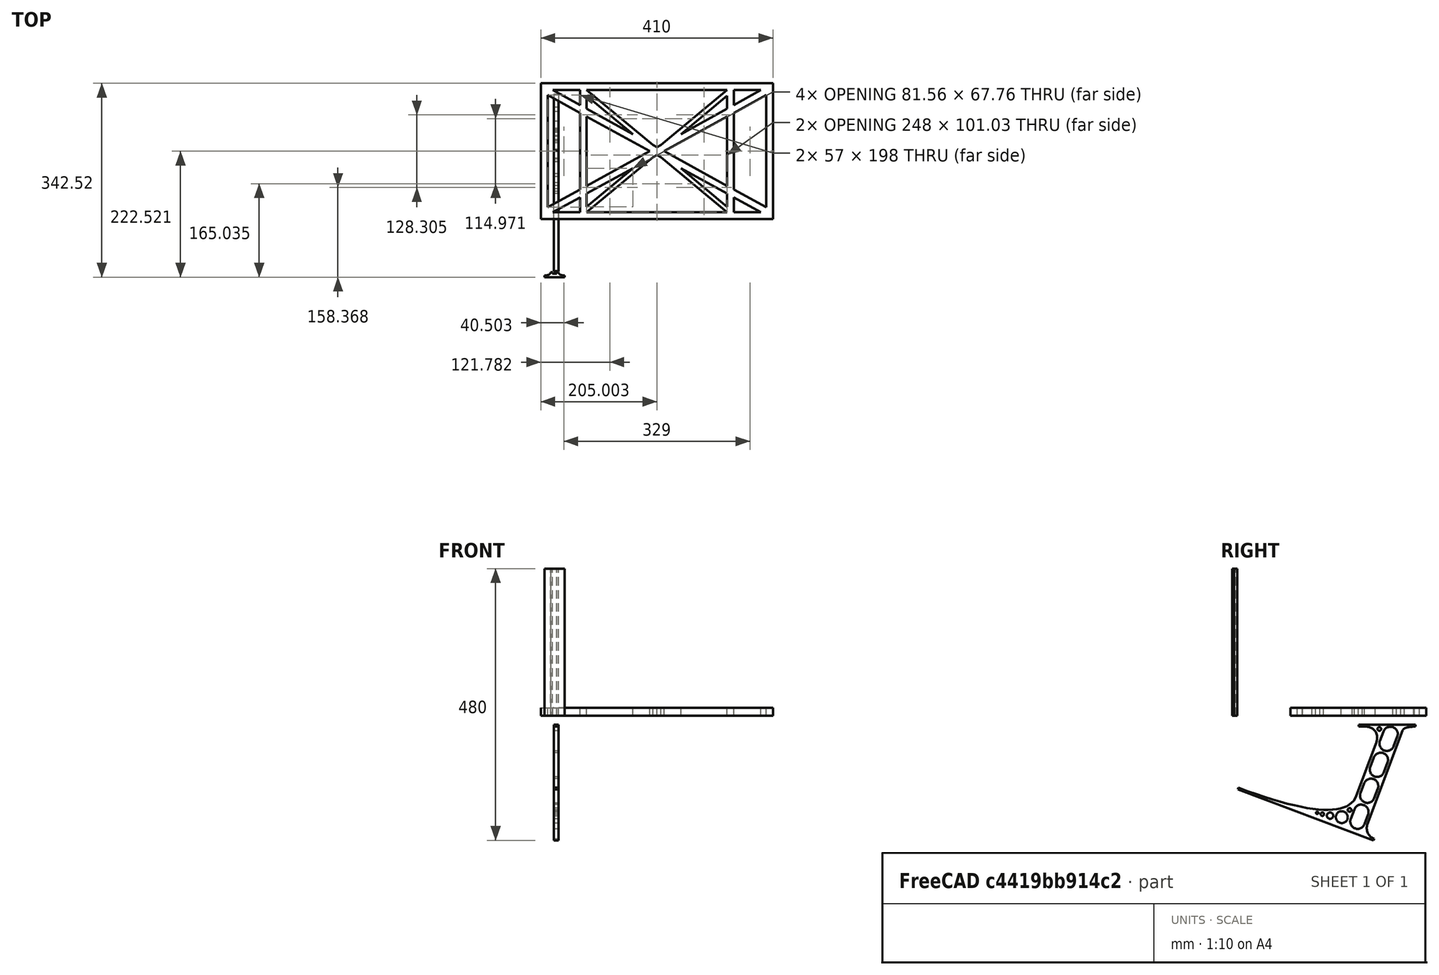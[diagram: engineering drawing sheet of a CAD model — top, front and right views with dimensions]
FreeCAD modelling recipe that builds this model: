
FCSTD DOCUMENT  (FreeCAD 0.19R0.19.2)
Label: laptopStand054
License: All rights reserved
LicenseURL: http://en.wikipedia.org/wiki/All_rights_reserved
objects: Sketcher::SketchObject×3, Part::Extrusion×3
note: 6 computed .brp shape members not serialized (recipe doc carries the construction recipe); baked Part::Feature solids carry a one-line shape summary decoded from their .brp

FEATURE [Sketcher::SketchObject] Sketch
  FullyConstrained = false
  sketch-geometry (92):
    g0: LineSegment StartX=-22.9272 StartY=136.221 StartZ=0 EndX=387.073 EndY=136.221 EndZ=0
    g1: LineSegment StartX=-22.9272 StartY=-103.779 StartZ=0 EndX=387.073 EndY=-103.779 EndZ=0
    g2: LineSegment StartX=375.073 StartY=115.221 StartZ=0 EndX=318.073 EndY=83.9235 EndZ=0
    g3: LineSegment StartX=-10.9272 StartY=-82.7794 StartZ=0 EndX=46.0728 EndY=-51.4823 EndZ=0
    g4: LineSegment StartX=-1.92719 StartY=124.221 StartZ=0 EndX=46.0728 EndY=97.8651 EndZ=0
    g5: LineSegment StartX=366.073 StartY=-91.7794 StartZ=0 EndX=318.073 EndY=-65.424 EndZ=0
    g6: LineSegment StartX=-10.9272 StartY=115.221 StartZ=0 EndX=-10.9272 EndY=-82.7794 EndZ=0
    g7: LineSegment StartX=375.073 StartY=-82.7794 StartZ=0 EndX=375.073 EndY=115.221 EndZ=0
    g8: LineSegment StartX=-1.92719 StartY=-91.7794 StartZ=0 EndX=46.0728 EndY=-91.7794 EndZ=0
    g9: LineSegment StartX=318.073 StartY=124.221 StartZ=0 EndX=366.073 EndY=124.221 EndZ=0
    g10: LineSegment StartX=306.073 StartY=-81.8102 StartZ=0 EndX=224.513 EndY=-14.0532 EndZ=0
    g11: LineSegment StartX=58.0728 StartY=114.251 StartZ=0 EndX=139.632 EndY=46.4944 EndZ=0
    g12: LineSegment StartX=306.073 StartY=124.221 StartZ=0 EndX=189.124 EndY=27.0628 EndZ=0
    g13: LineSegment StartX=58.0728 StartY=-91.7794 StartZ=0 EndX=175.022 EndY=5.37834 EndZ=0
    g14: LineSegment StartX=46.0728 StartY=124.221 StartZ=0 EndX=46.0728 EndY=97.8651 EndZ=0
    g15: LineSegment StartX=58.0728 StartY=-81.8102 StartZ=0 EndX=58.0728 EndY=-58.8351 EndZ=0
    g16: LineSegment StartX=318.073 StartY=124.221 StartZ=0 EndX=318.073 EndY=97.8651 EndZ=0
    g17: LineSegment StartX=306.073 StartY=114.251 StartZ=0 EndX=306.073 EndY=91.2763 EndZ=0
    g18: LineSegment StartX=224.513 StartY=46.4944 StartZ=0 EndX=306.073 EndY=114.251 EndZ=0
    g19: LineSegment StartX=175.022 StartY=27.0628 StartZ=0 EndX=58.0728 EndY=124.221 EndZ=0
    g20: LineSegment StartX=169.377 StartY=16.2206 StartZ=0 EndX=58.0728 EndY=77.3346 EndZ=0
    g21: LineSegment StartX=139.632 StartY=-14.0532 StartZ=0 EndX=58.0728 EndY=-81.8102 EndZ=0
    g22: LineSegment StartX=194.768 StartY=16.2206 StartZ=0 EndX=306.073 EndY=-44.8935 EndZ=0
    g23: LineSegment StartX=224.513 StartY=46.4944 StartZ=0 EndX=306.073 EndY=91.2763 EndZ=0
    g24: LineSegment StartX=139.632 StartY=-14.0532 StartZ=0 EndX=58.0728 EndY=-58.8351 EndZ=0
    g25: LineSegment StartX=189.124 StartY=5.37834 StartZ=0 EndX=306.073 EndY=-91.7794 EndZ=0
    g26: LineSegment StartX=306.073 StartY=77.3346 StartZ=0 EndX=306.073 EndY=-44.8935 EndZ=0
    g27: LineSegment StartX=318.073 StartY=83.9235 StartZ=0 EndX=318.073 EndY=-51.4823 EndZ=0
    g28: LineSegment StartX=318.073 StartY=97.8651 StartZ=0 EndX=366.073 EndY=124.221 EndZ=0
    g29: LineSegment StartX=306.073 StartY=77.3346 StartZ=0 EndX=194.768 EndY=16.2206 EndZ=0
    g30: LineSegment StartX=306.073 StartY=-58.8351 StartZ=0 EndX=224.513 EndY=-14.0532 EndZ=0
    g31: LineSegment StartX=306.073 StartY=-58.8351 StartZ=0 EndX=306.073 EndY=-81.8102 EndZ=0
    g32: LineSegment StartX=318.073 StartY=-51.4823 StartZ=0 EndX=375.073 EndY=-82.7794 EndZ=0
    g33: LineSegment StartX=318.073 StartY=-65.424 StartZ=0 EndX=318.073 EndY=-91.7794 EndZ=0
    g34: LineSegment StartX=318.073 StartY=-91.7794 StartZ=0 EndX=366.073 EndY=-91.7794 EndZ=0
    g35: LineSegment StartX=58.0728 StartY=-44.8935 StartZ=0 EndX=58.0728 EndY=77.3346 EndZ=0
    g36: LineSegment StartX=46.0728 StartY=-65.424 StartZ=0 EndX=-1.92719 EndY=-91.7794 EndZ=0
    g37: LineSegment StartX=46.0728 StartY=-65.424 StartZ=0 EndX=46.0728 EndY=-91.7794 EndZ=0
    g38: LineSegment StartX=58.0728 StartY=-44.8935 StartZ=0 EndX=169.377 EndY=16.2206 EndZ=0
    g39: LineSegment StartX=58.0728 StartY=91.2763 StartZ=0 EndX=58.0728 EndY=114.251 EndZ=0
    g40: LineSegment StartX=46.0728 StartY=83.9235 StartZ=0 EndX=46.0728 EndY=-51.4823 EndZ=0
    g41: LineSegment StartX=46.0728 StartY=124.221 StartZ=0 EndX=-1.92719 EndY=124.221 EndZ=0
    g42: LineSegment StartX=58.0728 StartY=91.2763 StartZ=0 EndX=139.632 EndY=46.4944 EndZ=0
    g43: LineSegment StartX=46.0728 StartY=83.9235 StartZ=0 EndX=-10.9272 EndY=115.221 EndZ=0
    g44: LineSegment StartX=-22.9272 StartY=136.221 StartZ=0 EndX=-42.9272 EndY=136.221 EndZ=0
    g45: LineSegment StartX=387.073 StartY=136.221 StartZ=0 EndX=407.073 EndY=136.221 EndZ=0
    g46: LineSegment StartX=-42.9272 StartY=136.221 StartZ=0 EndX=-42.9272 EndY=-103.779 EndZ=0
    g47: LineSegment StartX=-22.9272 StartY=-103.779 StartZ=0 EndX=-42.9272 EndY=-103.779 EndZ=0
    g48: LineSegment StartX=407.073 StartY=136.221 StartZ=0 EndX=407.073 EndY=-103.779 EndZ=0
    g49: LineSegment StartX=387.073 StartY=-103.779 StartZ=0 EndX=407.073 EndY=-103.779 EndZ=0
    g50: LineSegment StartX=179.022 StartY=27.0628 StartZ=0 EndX=179.022 EndY=124.221 EndZ=0
    g51: LineSegment StartX=185.124 StartY=27.0628 StartZ=0 EndX=185.124 EndY=124.221 EndZ=0
    g52: ArcOfCircle CenterX=-26.9272 CenterY=22.1087 CenterZ=0 NormalX=0 NormalY=0 NormalZ=1 AngleXU=0 Radius=8 StartAngle=1e-16 EndAngle=3.14159
    g53: ArcOfCircle CenterX=-26.9272 CenterY=-83.7794 CenterZ=0 NormalX=0 NormalY=0 NormalZ=1 AngleXU=0 Radius=8 StartAngle=3.14159 EndAngle=6.28319
    g54: LineSegment StartX=-34.9272 StartY=22.1087 StartZ=0 EndX=-34.9272 EndY=-83.7794 EndZ=0
    g55: LineSegment StartX=-18.9272 StartY=22.1087 StartZ=0 EndX=-18.9272 EndY=-83.7794 EndZ=0
    g56: LineSegment StartX=185.124 StartY=-91.7794 StartZ=0 EndX=306.073 EndY=-91.7794 EndZ=0
    g57: LineSegment StartX=179.022 StartY=-91.7794 StartZ=0 EndX=58.0728 EndY=-91.7794 EndZ=0
    g58: LineSegment StartX=306.073 StartY=124.221 StartZ=0 EndX=185.124 EndY=124.221 EndZ=0
    g59: LineSegment StartX=179.022 StartY=124.221 StartZ=0 EndX=58.0728 EndY=124.221 EndZ=0
    g60: ArcOfCircle CenterX=391.073 CenterY=22.1087 CenterZ=0 NormalX=0 NormalY=0 NormalZ=1 AngleXU=0 Radius=8 StartAngle=-4.4e-15 EndAngle=3.14159
    g61: LineSegment StartX=399.073 StartY=22.1087 StartZ=0 EndX=399.073 EndY=-83.7794 EndZ=0
    g62: LineSegment StartX=383.073 StartY=22.1087 StartZ=0 EndX=383.073 EndY=-83.7794 EndZ=0
    g63: ArcOfCircle CenterX=391.073 CenterY=-83.7794 CenterZ=0 NormalX=0 NormalY=0 NormalZ=1 AngleXU=0 Radius=8 StartAngle=3.14159 EndAngle=6.28319
    g64: Circle CenterX=175.022 CenterY=27.0628 CenterZ=0 NormalX=0 NormalY=0 NormalZ=1 AngleXU=0 Radius=1
    g65: Circle CenterX=179.022 CenterY=24.8665 CenterZ=0 NormalX=0 NormalY=0 NormalZ=1 AngleXU=0 Radius=1
    g66: Circle CenterX=179.022 CenterY=27.0628 CenterZ=0 NormalX=0 NormalY=0 NormalZ=1 AngleXU=0 Radius=1
    g67: BSplineCurve PolesCount=3 KnotsCount=2 Degree=2 IsPeriodic=0
    g68: GeomPoint X=175.022 Y=27.0628 Z=0
    g69: GeomPoint X=179.022 Y=27.0628 Z=0
    g70: Circle CenterX=189.124 CenterY=27.0628 CenterZ=0 NormalX=0 NormalY=0 NormalZ=1 AngleXU=0 Radius=1
    g71: Circle CenterX=185.124 CenterY=24.8665 CenterZ=0 NormalX=0 NormalY=0 NormalZ=1 AngleXU=0 Radius=1
    g72: Circle CenterX=185.124 CenterY=27.0628 CenterZ=0 NormalX=0 NormalY=0 NormalZ=1 AngleXU=0 Radius=1
    g73: BSplineCurve PolesCount=3 KnotsCount=2 Degree=2 IsPeriodic=0
    g74: GeomPoint X=189.124 Y=27.0628 Z=0
    g75: GeomPoint X=185.124 Y=27.0628 Z=0
    g76: Circle CenterX=175.022 CenterY=5.37834 CenterZ=0 NormalX=0 NormalY=0 NormalZ=1 AngleXU=0 Radius=1
    g77: Circle CenterX=179.022 CenterY=7.57463 CenterZ=0 NormalX=0 NormalY=0 NormalZ=1 AngleXU=0 Radius=1
    g78: Circle CenterX=179.022 CenterY=5.34704 CenterZ=0 NormalX=0 NormalY=0 NormalZ=1 AngleXU=0 Radius=1
    g79: BSplineCurve PolesCount=3 KnotsCount=2 Degree=2 IsPeriodic=0
    g80: GeomPoint X=175.022 Y=5.37834 Z=0
    g81: GeomPoint X=179.022 Y=5.34704 Z=0
    g82: Circle CenterX=189.124 CenterY=5.37834 CenterZ=0 NormalX=0 NormalY=0 NormalZ=1 AngleXU=0 Radius=1
    g83: Circle CenterX=185.124 CenterY=7.57463 CenterZ=0 NormalX=0 NormalY=0 NormalZ=1 AngleXU=0 Radius=1
    g84: Circle CenterX=185.124 CenterY=5.34704 CenterZ=0 NormalX=0 NormalY=0 NormalZ=1 AngleXU=0 Radius=1
    g85: BSplineCurve PolesCount=3 KnotsCount=2 Degree=2 IsPeriodic=0
    g86: GeomPoint X=189.124 Y=5.37834 Z=0
    g87: GeomPoint X=185.124 Y=5.34704 Z=0
    g88: LineSegment StartX=179.022 StartY=5.34704 StartZ=0 EndX=179.022 EndY=-91.7794 EndZ=0
    g89: LineSegment StartX=185.124 StartY=-91.7794 StartZ=0 EndX=185.124 EndY=5.34704 EndZ=0
    g90: LineSegment StartX=165.377 StartY=16.2206 StartZ=0 EndX=169.377 EndY=16.2206 EndZ=0
    g91: LineSegment StartX=194.768 StartY=16.2206 StartZ=0 EndX=198.768 EndY=16.2206 EndZ=0
  constraints (182):
    c: Horizontal(g0)
    c: Distance(g0) = 410
    c: Horizontal(g1)
    c: Block(g0)
    c: Horizontal(g8)
    c: Horizontal(g9)
    c: Tangent(g5,g20)
    c: PointOnObject(g20,g3)
    c: PointOnObject(g22,g2)
    c: Coincident(g42,g11)
    c: Coincident(g18,g23)
    c: Coincident(g24,g21)
    c: Coincident(g30,g10)
    c: Coincident(g18,g17)
    c: Tangent(g17,g26)
    c: Tangent(g16,g27)
    c: Coincident(g23,g17)
    c: Tangent(g23,g28)
    c: Coincident(g2,g27)
    c: Coincident(g29,g26)
    c: Tangent(g2,g29)
    c: Coincident(g31,g10)
    c: Tangent(g5,g30)
    c: Tangent(g26,g31)
    c: Coincident(g22,g26)
    c: Tangent(g22,g32)
    c: Coincident(g27,g32)
    c: Coincident(g33,g5)
    c: Tangent(g27,g33)
    c: Coincident(g21,g15)
    c: Tangent(g15,g35)
    c: Coincident(g24,g15)
    c: Tangent(g24,g36)
    c: Coincident(g37,g36)
    c: Tangent(g14,g37)
    c: Coincident(g3,g40)
    c: Coincident(g38,g35)
    c: Tangent(g3,g38)
    c: Tangent(g35,g39)
    c: Tangent(g14,g40)
    c: Coincident(g11,g39)
    c: Coincident(g4,g14)
    c: Coincident(g42,g39)
    c: Tangent(g4,g42)
    c: Coincident(g20,g35)
    c: Coincident(g43,g40)
    c: Tangent(g20,g43)
    c: Block(g19)
    c: Block(g12)
    c: Block(g16)
    c: Block(g28)
    c: Block(g2)
    c: Block(g32)
    c: Block(g7)
    c: Block(g30)
    c: Block(g31)
    c: Block(g5)
    c: Block(g33)
    c: Block(g18)
    c: Block(g25)
    c: Block(g13)
    c: Block(g24)
    c: Block(g21)
    c: Block(g37)
    c: Block(g36)
    c: Block(g3)
    c: Block(g6)
    c: Block(g43)
    c: Block(g4)
    c: Block(g14)
    c: Block(g11)
    c: Block(g39)
    c: Block(g29)
    c: Block(g26)
    c: Block(g20)
    c: Block(g38)
    c: Block(g41)
    c: Block(g9)
    c: Block(g34)
    c: Block(g8)
    c: Horizontal(g44)
    c: Distance(g44) = 20
    c: Coincident(g45,g0)
    c: Horizontal(g45)
    c: Distance(g45) = 20
    c: Coincident(g46,g44)
    c: Vertical(g46)
    c: Horizontal(g47)
    c: Coincident(g47,g46)
    c: Coincident(g48,g45)
    c: Vertical(g48)
    c: Coincident(g49,g1)
    c: Horizontal(g49)
    c: Coincident(g49,g48)
    c: Block(g48)
    c: Block(g47)
    c: Block(g46)
    c: Block(g1)
    c: Vertical(g50)
    c: Vertical(g51)
    c: Block(g50)
    c: Block(g51)
    c: Tangent(g52,g55) = 1.5708
    c: Tangent(g52,g54) = -1.5708
    c: Tangent(g54,g53) = -1.5708
    c: Tangent(g55,g53) = 1.5708
    c: Vertical(g54)
    c: Equal(g52,g53)
    c: Block(g55)
    c: Block(g54)
    c: Coincident(g56,g25)
    c: Horizontal(g56)
    c: Coincident(g57,g13)
    c: Horizontal(g57)
    c: Coincident(g58,g12)
    c: Coincident(g58,g51)
    c: Horizontal(g58)
    c: Coincident(g59,g50)
    c: Coincident(g59,g19)
    c: Horizontal(g59)
    c: Distance(g49) = 20
    c: Distance(g1) = 410
    c: Tangent(g60,g61) = 1.5708
    c: Tangent(g61,g63) = 1.5708
    c: Equal(g60,g63)
    c: Coincident(g62,g60)
    c: Coincident(g62,g63)
    c: Vertical(g62)
    c: Block(g61)
    c: Block(g62)
    c: Block(g22)
    c: Coincident(g67,g19)
    c: Weight(g64) = 1
    c: Equal(g64,g65)
    c: Equal(g64,g66)
    c: Coincident(g67,g50)
    c: InternalAlignment(g64,g67)
    c: InternalAlignment(g65,g67)
    c: InternalAlignment(g66,g67)
    c: InternalAlignment(g68,g67)
    c: InternalAlignment(g69,g67)
    c: Coincident(g73,g12)
    c: Weight(g70) = 1
    c: Equal(g70,g71)
    c: Equal(g70,g72)
    c: Coincident(g73,g51)
    c: InternalAlignment(g70,g73)
    c: InternalAlignment(g71,g73)
    c: InternalAlignment(g72,g73)
    c: InternalAlignment(g74,g73)
    c: InternalAlignment(g75,g73)
    c: Block(g73)
    c: Block(g67)
    c: Coincident(g79,g13)
    c: Weight(g76) = 1
    c: Equal(g76,g77)
    c: Equal(g76,g78)
    c: InternalAlignment(g76,g79)
    c: InternalAlignment(g77,g79)
    c: InternalAlignment(g78,g79)
    c: InternalAlignment(g80,g79)
    c: InternalAlignment(g81,g79)
    c: Weight(g82) = 1
    c: Equal(g82,g83)
    c: Equal(g82,g84)
    c: InternalAlignment(g82,g85)
    c: InternalAlignment(g83,g85)
    c: InternalAlignment(g84,g85)
    c: InternalAlignment(g86,g85)
    c: InternalAlignment(g87,g85)
    c: Block(g85)
    c: Block(g79)
    c: Coincident(g88,g79)
    c: Coincident(g88,g57)
    c: Vertical(g88)
    c: Coincident(g89,g56)
    c: Coincident(g89,g85)
    c: Vertical(g89)
    c: Horizontal(g90)
    c: Horizontal(g91)
    c: Coincident(g91,g22)
    c: Coincident(g90,g20)
FEATURE [Sketcher::SketchObject] Sketch001
  FullyConstrained = true
  MapMode = 4
  Placement = pos=(0,0,0) rot=(0.57735,0.57735,0.57735;2.0944rad)
  Support = -> [Sketch]
  sketch-geometry (46):
    g0: BSplineCurve PolesCount=3 KnotsCount=2 Degree=2 IsPeriodic=0
    g1: ArcOfCircle CenterX=73.122 CenterY=-32.2909 CenterZ=0 NormalX=0 NormalY=0 NormalZ=1 AngleXU=0 Radius=13 StartAngle=5.92268 EndAngle=9.06428
    g2: ArcOfCircle CenterX=66.7816 CenterY=-49.1439 CenterZ=0 NormalX=0 NormalY=0 NormalZ=1 AngleXU=0 Radius=13 StartAngle=2.78068 EndAngle=5.92131
    g3: ArcOfCircle CenterX=55.9263 CenterY=-78.1807 CenterZ=0 NormalX=0 NormalY=0 NormalZ=1 AngleXU=0 Radius=13 StartAngle=5.92268 EndAngle=9.06428
    g4: ArcOfCircle CenterX=49.5884 CenterY=-95.0342 CenterZ=0 NormalX=0 NormalY=0 NormalZ=1 AngleXU=0 Radius=13 StartAngle=2.78068 EndAngle=5.92131
    g5: ArcOfCircle CenterX=38.7206 CenterY=-124.067 CenterZ=0 NormalX=0 NormalY=0 NormalZ=1 AngleXU=0 Radius=13 StartAngle=5.92268 EndAngle=9.06428
    g6: ArcOfCircle CenterX=32.3875 CenterY=-140.92 CenterZ=0 NormalX=0 NormalY=0 NormalZ=1 AngleXU=0 Radius=13 StartAngle=2.78068 EndAngle=5.92131
    g7: ArcOfCircle CenterX=21.4715 CenterY=-169.934 CenterZ=0 NormalX=0 NormalY=0 NormalZ=1 AngleXU=0 Radius=13 StartAngle=5.92268 EndAngle=9.06428
    g8: ArcOfCircle CenterX=15.1336 CenterY=-186.787 CenterZ=0 NormalX=0 NormalY=0 NormalZ=1 AngleXU=0 Radius=13 StartAngle=2.78068 EndAngle=5.92131
    g9-g12: Circle x4 (B-spline internal-alignment scaffolding for g13; pole/knot coordinates omitted)
    g13: BSplineCurve PolesCount=4 KnotsCount=2 Degree=3 IsPeriodic=0
    g14: GeomPoint X=28.8094 Y=-19.0875 Z=0
    g15: GeomPoint X=47.0443 Y=-50.4712 Z=0
    g16: Circle CenterX=53.5586 CenterY=-23.2695 CenterZ=0 NormalX=0 NormalY=0 NormalZ=1 AngleXU=0 Radius=3.24518
    g17: Circle CenterX=-195.441 CenterY=-127.082 CenterZ=0 NormalX=0 NormalY=0 NormalZ=1 AngleXU=0 Radius=1
    g18: Circle CenterX=-8.24091 CenterY=-197.481 CenterZ=0 NormalX=0 NormalY=0 NormalZ=1 AngleXU=0 Radius=1
    g19: Circle CenterX=12.8789 CenterY=-141.321 CenterZ=0 NormalX=0 NormalY=0 NormalZ=1 AngleXU=0 Radius=1
    g20: BSplineCurve PolesCount=3 KnotsCount=2 Degree=2 IsPeriodic=0
    g21: GeomPoint X=-195.441 Y=-127.082 Z=0
    g22: GeomPoint X=12.8789 Y=-141.321 Z=0
    g23: Circle CenterX=-12.8016 CenterY=-179.036 CenterZ=0 NormalX=0 NormalY=0 NormalZ=1 AngleXU=0 Radius=10.5072
    g24: Circle CenterX=0.933922 CenterY=-166.43 CenterZ=0 NormalX=0 NormalY=0 NormalZ=1 AngleXU=0 Radius=3.26661
    g25: Circle CenterX=-33.5518 CenterY=-176.44 CenterZ=0 NormalX=0 NormalY=0 NormalZ=1 AngleXU=0 Radius=5.64388
    g26: Circle CenterX=-47.2366 CenterY=-173.859 CenterZ=0 NormalX=0 NormalY=0 NormalZ=1 AngleXU=0 Radius=3.01653
    g27: Circle CenterX=-56.2595 CenterY=-171.456 CenterZ=0 NormalX=0 NormalY=0 NormalZ=1 AngleXU=0 Radius=2.12826
    g28: ArcOfCircle CenterX=51.2151 CenterY=-198.473 CenterZ=0 NormalX=0 NormalY=0 NormalZ=1 AngleXU=0 Radius=20 StartAngle=2.78189 EndAngle=4.35269
    g29: LineSegment StartX=32.4951 StartY=-191.433 StartZ=0 EndX=94.6577 EndY=-26.1351 EndZ=0
    g30: LineSegment StartX=43.1192 StartY=-220.001 StartZ=0 EndX=-196.497 EndY=-129.89 EndZ=0
    g31: LineSegment StartX=43.1192 StartY=-220.001 StartZ=0 EndX=44.1752 EndY=-217.193 EndZ=0
    g32: LineSegment StartX=117.223 StartY=-19.0875 StartZ=0 EndX=117.223 EndY=-16.0875 EndZ=0
    g33: LineSegment StartX=117.223 StartY=-16.0875 StartZ=0 EndX=17.2232 EndY=-16.0875 EndZ=0
    g34: LineSegment StartX=17.2232 StartY=-16.0875 StartZ=0 EndX=17.2232 EndY=-19.0875 EndZ=0
    g35: LineSegment StartX=28.8094 StartY=-19.0875 StartZ=0 EndX=17.2232 EndY=-19.0875 EndZ=0
    g36: LineSegment StartX=47.0443 StartY=-50.4712 StartZ=0 EndX=12.8789 EndY=-141.321 EndZ=0
    g37: LineSegment StartX=-195.441 StartY=-127.082 StartZ=0 EndX=-196.497 EndY=-129.89 EndZ=0
    g38: LineSegment StartX=85.2864 StartY=-36.8765 StartZ=0 EndX=78.9396 EndY=-53.7463 EndZ=0
    g39: LineSegment StartX=60.9577 StartY=-27.7052 StartZ=0 EndX=54.6191 EndY=-44.5532 EndZ=0
    g40: LineSegment StartX=68.0907 StartY=-82.7664 StartZ=0 EndX=61.7465 EndY=-99.6365 EndZ=0
    g41: LineSegment StartX=43.7619 StartY=-73.595 StartZ=0 EndX=37.426 EndY=-90.4435 EndZ=0
    g42: LineSegment StartX=50.885 StartY=-128.652 StartZ=0 EndX=44.5456 EndY=-145.522 EndZ=0
    g43: LineSegment StartX=26.5562 StartY=-119.481 StartZ=0 EndX=20.2251 EndY=-136.329 EndZ=0
    g44: LineSegment StartX=9.3071 StartY=-165.349 StartZ=0 EndX=2.97115 EndY=-182.197 EndZ=0
    g45: LineSegment StartX=33.6358 StartY=-174.52 StartZ=0 EndX=27.2917 EndY=-191.39 EndZ=0
  constraints (70):
    c: Block(g0)
    c: Block(g1)
    c: Block(g2)
    c: Block(g4)
    c: Block(g3)
    c: Block(g6)
    c: Block(g5)
    c: Block(g8)
    c: Block(g7)
    c: Weight(g9) = 1
    c: Equal(g9,g10)
    c: Equal(g9,g11)
    c: Equal(g9,g12)
    c: InternalAlignment(g9-g12 -> g13) x4
    c: InternalAlignment(g14,g13)
    c: InternalAlignment(g15,g13)
    c: Block(g16)
    c: Weight(g17) = 1
    c: Equal(g17,g18)
    c: Equal(g17,g19)
    c: InternalAlignment(g17,g20)
    c: InternalAlignment(g18,g20)
    c: InternalAlignment(g19,g20)
    c: InternalAlignment(g21,g20)
    c: InternalAlignment(g22,g20)
    c: Block(g20)
    c: Block(g23)
    c: Block(g24)
    c: Block(g25)
    c: Block(g26)
    c: Block(g27)
    c: Block(g28)
    c: Coincident(g29,g28)
    c: Coincident(g29,g0)
    c: Block(g13)
    c: Coincident(g31,g30)
    c: Coincident(g31,g28)
    c: Block(g31)
    c: Coincident(g32,g0)
    c: Vertical(g32)
    c: Coincident(g33,g32)
    c: Horizontal(g33)
    c: Coincident(g34,g33)
    c: Vertical(g34)
    c: Block(g33)
    c: Coincident(g35,g13)
    c: Coincident(g35,g34)
    c: Horizontal(g35)
    c: Coincident(g36,g13)
    c: Coincident(g36,g20)
    c: Coincident(g37,g20)
    c: Coincident(g37,g30)
    c: Block(g30)
    c: Coincident(g38,g1)
    c: Coincident(g38,g2)
    c: Coincident(g39,g1)
    c: Coincident(g39,g2)
    c: Coincident(g40,g3)
    c: Coincident(g40,g4)
    c: Coincident(g41,g3)
    c: Coincident(g41,g4)
    c: Coincident(g42,g5)
    c: Coincident(g42,g6)
    c: Coincident(g43,g5)
    c: Coincident(g43,g6)
    c: Coincident(g44,g7)
    c: Coincident(g44,g8)
    c: Coincident(g45,g7)
    c: Coincident(g45,g8)
    c: Distance(g30) = 256
FEATURE [Part::Extrusion] Extrude002
  Base = -> Sketch001
  Dir = (1,0,0)
  DirMode = 2
  FaceMakerClass = Part::FaceMakerBullseye
  LengthFwd = 8
  LengthRev = 0
  Solid = true
  Symmetric = false
FEATURE [Sketcher::SketchObject] Sketch002
  FullyConstrained = true
  sketch-geometry (20):
    g0: LineSegment StartX=-2.77179 StartY=-200.304 StartZ=0 EndX=5.22821 EndY=-200.304 EndZ=0
    g1: LineSegment StartX=5.22821 StartY=-200.304 StartZ=0 EndX=5.22821 EndY=-197.304 EndZ=0
    g2: LineSegment StartX=-2.77179 StartY=-200.304 StartZ=0 EndX=-2.77179 EndY=-197.304 EndZ=0
    g3: LineSegment StartX=5.22821 StartY=-197.304 StartZ=0 EndX=8.22821 EndY=-197.304 EndZ=0
    g4: LineSegment StartX=-2.77179 StartY=-197.304 StartZ=0 EndX=-5.77179 EndY=-197.304 EndZ=0
    g5: LineSegment StartX=19.2282 StartY=-203.304 StartZ=0 EndX=19.2282 EndY=-206.304 EndZ=0
    g6: LineSegment StartX=-16.7718 StartY=-203.304 StartZ=0 EndX=-16.7718 EndY=-206.304 EndZ=0
    g7: LineSegment StartX=-16.7718 StartY=-206.304 StartZ=0 EndX=19.2282 EndY=-206.304 EndZ=0
    g8: Circle CenterX=-16.7718 CenterY=-203.304 CenterZ=0 NormalX=0 NormalY=0 NormalZ=1 AngleXU=0 Radius=1
    g9: Circle CenterX=-5.77179 CenterY=-203.304 CenterZ=0 NormalX=0 NormalY=0 NormalZ=1 AngleXU=0 Radius=1
    g10: Circle CenterX=-5.77179 CenterY=-197.304 CenterZ=0 NormalX=0 NormalY=0 NormalZ=1 AngleXU=0 Radius=1
    g11: BSplineCurve PolesCount=3 KnotsCount=2 Degree=2 IsPeriodic=0
    g12: GeomPoint X=-16.7718 Y=-203.304 Z=0
    g13: GeomPoint X=-5.77179 Y=-197.304 Z=0
    g14: Circle CenterX=19.2282 CenterY=-203.304 CenterZ=0 NormalX=0 NormalY=0 NormalZ=1 AngleXU=0 Radius=1
    g15: Circle CenterX=8.22821 CenterY=-203.304 CenterZ=0 NormalX=0 NormalY=0 NormalZ=1 AngleXU=0 Radius=1
    g16: Circle CenterX=8.22821 CenterY=-197.304 CenterZ=0 NormalX=0 NormalY=0 NormalZ=1 AngleXU=0 Radius=1
    g17: BSplineCurve PolesCount=3 KnotsCount=2 Degree=2 IsPeriodic=0
    g18: GeomPoint X=19.2282 Y=-203.304 Z=0
    g19: GeomPoint X=8.22821 Y=-197.304 Z=0
  constraints (41):
    c: Horizontal(g0)
    c: Distance(g0) = 8
    c: Coincident(g1,g0)
    c: Vertical(g1)
    c: Distance(g1) = 3
    c: Coincident(g2,g0)
    c: Vertical(g2)
    c: Distance(g2) = 3
    c: Coincident(g3,g1)
    c: Horizontal(g3)
    c: Distance(g3) = 3
    c: Coincident(g4,g2)
    c: Horizontal(g4)
    c: Distance(g4) = 3
    c: Vertical(g5)
    c: Vertical(g6)
    c: Coincident(g7,g6)
    c: Coincident(g7,g5)
    c: Weight(g8) = 1
    c: Equal(g8,g9)
    c: Equal(g8,g10)
    c: Coincident(g11,g4)
    c: InternalAlignment(g8,g11)
    c: InternalAlignment(g9,g11)
    c: InternalAlignment(g10,g11)
    c: InternalAlignment(g12,g11)
    c: InternalAlignment(g13,g11)
    c: Coincident(g17,g5)
    c: Weight(g14) = 1
    c: Equal(g14,g15)
    c: Equal(g14,g16)
    c: Coincident(g17,g3)
    c: InternalAlignment(g14,g17)
    c: InternalAlignment(g15,g17)
    c: InternalAlignment(g16,g17)
    c: InternalAlignment(g18,g17)
    c: InternalAlignment(g19,g17)
    c: Block(g7)
    c: Block(g17)
    c: Block(g11)
    c: Block(g6)
FEATURE [Part::Extrusion] Extrude003
  Base = -> Sketch002
  Dir = (0,0,1)
  DirMode = 2
  FaceMakerClass = Part::FaceMakerBullseye
  LengthFwd = 260
  LengthRev = 0
  Solid = true
  Symmetric = false
FEATURE [Part::Extrusion] Extrude
  Base = -> Sketch
  Dir = (0,0,1)
  DirMode = 2
  FaceMakerClass = Part::FaceMakerBullseye
  LengthFwd = 14
  LengthRev = 0
  Solid = true
  Symmetric = false
